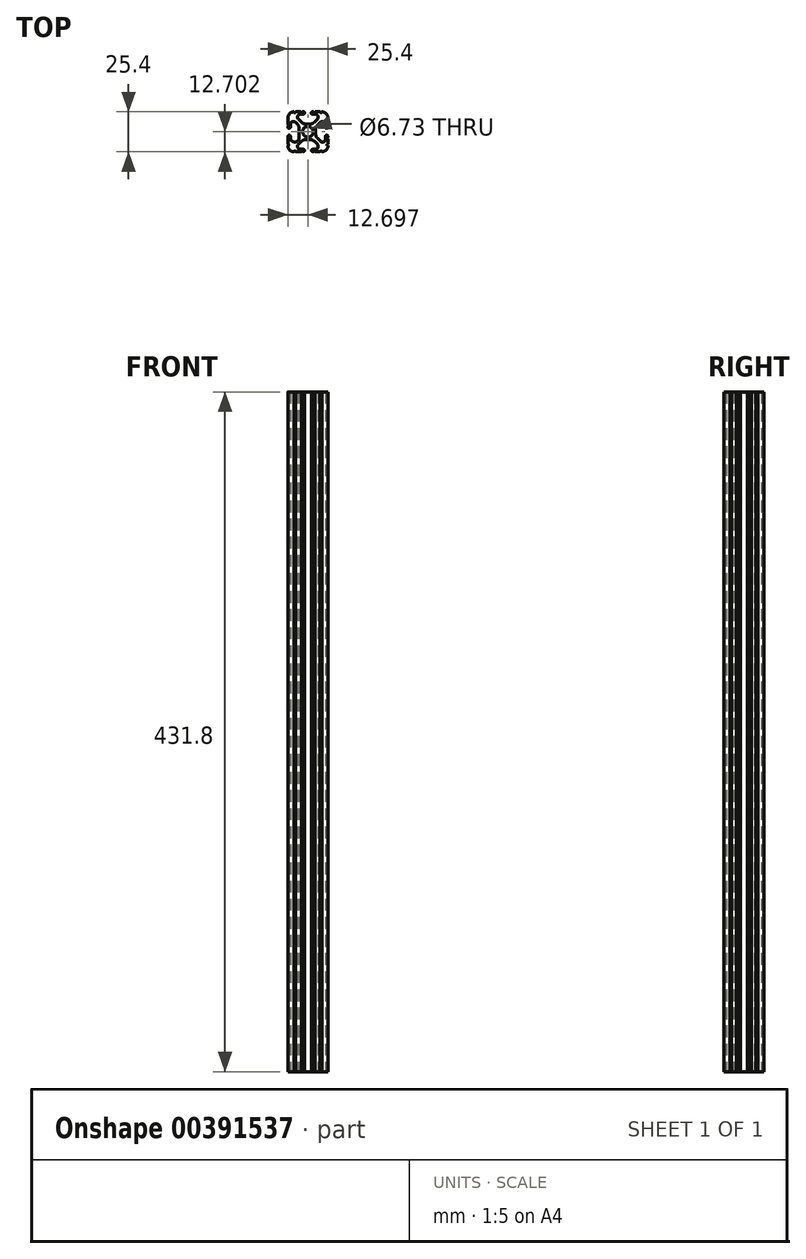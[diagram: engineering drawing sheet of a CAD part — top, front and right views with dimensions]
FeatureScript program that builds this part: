
annotation { "Feature Type Name" : "Feature", "Feature Type Description" : "" }
export const myFeature = defineFeature(function(context is Context, id is Id, definition is map)
    precondition{}
    {
        {
            var Q0;
            Q0=qCreatedBy(makeId("Top.planeOp"),FACE);
            var sketch = newSketch(context, id + "F0", { "sketchPlane" : qUnion([Q0])});
            skCircle(sketch, "E0", {"center": v(-11.44, 9.32) * mm, "radius": 3.36 * mm});
            skLineSegment(sketch, "E1.bottom", {"start": v(-9.99, 14.26) * mm, "end": v(-12.9, 14.26) * mm});
            skLineSegment(sketch, "E1.top", {"start": v(-9.99, 4.38) * mm, "end": v(-12.9, 4.38) * mm});
            skLineSegment(sketch, "E1.left", {"start": v(-6.5, 10.78) * mm, "end": v(-6.5, 7.86) * mm});
            skLineSegment(sketch, "E1.right", {"start": v(-16.98, 11.37) * mm, "end": v(-16.98, 5.6) * mm});
            skPoint(sketch, "E2.visualSharp", {"position": v(-24.14, 22.02) * mm});
            skPoint(sketch, "E3.visualSharp", {"position": v(1.26, 22.02) * mm});
            skPoint(sketch, "E4.visualSharp", {"position": v(1.26, -3.38) * mm});
            skPoint(sketch, "E5.visualSharp", {"position": v(-24.14, -3.38) * mm});
            skLineSegment(sketch, "E6.0", {"start": v(-17.44, 17.22) * mm, "end": v(-15.6, 15.38) * mm});
            skLineSegment(sketch, "E7.0", {"start": v(-19.34, 15.32) * mm, "end": v(-18.1, 14.07) * mm});
            skPoint(sketch, "E8.orphan", {"position": v(-22.6, -1.83) * mm});
            skPoint(sketch, "E9.orphan", {"position": v(-22.6, 20.47) * mm});
            skPoint(sketch, "E10.orphan", {"position": v(-0.3, 20.47) * mm});
            skPoint(sketch, "E11.orphan", {"position": v(-0.3, -1.83) * mm});
            skLineSegment(sketch, "E12", {"start": v(-7.3, 3.27) * mm, "end": v(-5.45, 1.42) * mm});
            skLineSegment(sketch, "E13.0", {"start": v(-17.44, 1.42) * mm, "end": v(-15.6, 3.27) * mm});
            skLineSegment(sketch, "E14.0", {"start": v(-7.3, 15.38) * mm, "end": v(-5.45, 17.22) * mm});
            skPoint(sketch, "E15.visualSharp", {"position": v(-22.6, 18.57) * mm});
            skArc(sketch, "E15.filletArc", {"start": v(-19.34, 15.32) * mm, "mid": v(-21.42, 15.73) * mm, "end": v(-22.6, 13.97) * mm});
            skPoint(sketch, "E16.visualSharp", {"position": v(-20.7, 20.47) * mm});
            skArc(sketch, "E16.filletArc", {"start": v(-16.1, 20.47) * mm, "mid": v(-17.85, 19.3) * mm, "end": v(-17.44, 17.22) * mm});
            skPoint(sketch, "E17.visualSharp", {"position": v(-4.09, 20.47) * mm});
            skLineSegment(sketch, "E18", {"start": v(-16.1, 20.47) * mm, "end": v(-14.33, 20.47) * mm});
            skLineSegment(sketch, "E19", {"start": v(-22.6, 13.97) * mm, "end": v(-22.6, 12.24) * mm});
            skLineSegment(sketch, "E20", {"start": v(-6.8, -1.83) * mm, "end": v(-8.53, -1.83) * mm});
            skArc(sketch, "E21.filletArc", {"start": v(-5.45, 17.22) * mm, "mid": v(-5.03, 19.3) * mm, "end": v(-6.8, 20.47) * mm});
            skPoint(sketch, "E22.visualSharp", {"position": v(-0.3, 0.08) * mm});
            skPoint(sketch, "E23.visualSharp", {"position": v(-2.2, -1.83) * mm});
            skArc(sketch, "E23.filletArc", {"start": v(-6.8, -1.83) * mm, "mid": v(-5.04, -0.65) * mm, "end": v(-5.45, 1.42) * mm});
            skArc(sketch, "E24.filletArc", {"start": v(-17.44, 1.42) * mm, "mid": v(-17.85, -0.65) * mm, "end": v(-16.1, -1.83) * mm});
            skArc(sketch, "E25.filletArc", {"start": v(-22.6, 5.6) * mm, "mid": v(-19.79, 2.8) * mm, "end": v(-16.98, 5.6) * mm});
            skLineSegment(sketch, "E26.bottom", {"start": v(-3.64, -3.38) * mm, "end": v(-6.8, -3.38) * mm});
            skLineSegment(sketch, "E26.top", {"start": v(-3.66, 22.02) * mm, "end": v(-6.8, 22.02) * mm});
            skLineSegment(sketch, "E26.left", {"start": v(1.26, 1.52) * mm, "end": v(1.26, 4.67) * mm});
            skArc(sketch, "E27.filletArc", {"start": v(-24.14, 0.43) * mm, "mid": v(-23.03, -2.26) * mm, "end": v(-20.33, -3.38) * mm});
            skArc(sketch, "E28.filletArc", {"start": v(-2.55, -3.38) * mm, "mid": v(0.14, -2.26) * mm, "end": v(1.26, 0.43) * mm});
            skArc(sketch, "E29.filletArc", {"start": v(1.26, 18.21) * mm, "mid": v(0.14, 20.9) * mm, "end": v(-2.55, 22.02) * mm});
            skArc(sketch, "E30.filletArc", {"start": v(-20.33, 22.02) * mm, "mid": v(-23.03, 20.9) * mm, "end": v(-24.14, 18.21) * mm});
            skPoint(sketch, "E31.newPointA", {"position": v(-16.38, 4.38) * mm});
            skArc(sketch, "E31.filletArc", {"start": v(-12.9, 4.38) * mm, "mid": v(-14.36, 4.1) * mm, "end": v(-15.6, 3.27) * mm});
            skPoint(sketch, "E32.newPointA", {"position": v(-6.5, 4.38) * mm});
            skArc(sketch, "E32.filletArc", {"start": v(-7.3, 3.27) * mm, "mid": v(-8.53, 4.1) * mm, "end": v(-9.99, 4.38) * mm});
            skArc(sketch, "E33.filletArc", {"start": v(-6.5, 7.86) * mm, "mid": v(-6.21, 6.4) * mm, "end": v(-5.39, 5.17) * mm});
            skArc(sketch, "E34.filletArc", {"start": v(-5.39, 13.47) * mm, "mid": v(-6.21, 12.24) * mm, "end": v(-6.5, 10.78) * mm});
            skPoint(sketch, "E35.newPointB", {"position": v(-6.5, 14.26) * mm});
            skArc(sketch, "E35.filletArc", {"start": v(-9.99, 14.26) * mm, "mid": v(-8.53, 14.55) * mm, "end": v(-7.3, 15.38) * mm});
            skPoint(sketch, "E36.newPointB", {"position": v(-16.38, 14.26) * mm});
            skArc(sketch, "E36.filletArc", {"start": v(-15.6, 15.38) * mm, "mid": v(-14.36, 14.55) * mm, "end": v(-12.9, 14.26) * mm});
            skArc(sketch, "E37.filletArc", {"start": v(-16.98, 11.37) * mm, "mid": v(-17.27, 12.83) * mm, "end": v(-18.1, 14.07) * mm});
            skLineSegment(sketch, "E38.filletArc", {"start": v(-16.98, 3.06) * mm, "end": v(-16.98, 3.06) * mm});
            skLineSegment(sketch, "E39", {"start": v(-5.39, 5.17) * mm, "end": v(-3.54, 3.33) * mm});
            skPoint(sketch, "E40.visualSharp", {"position": v(-0.3, 18.57) * mm});
            skArc(sketch, "E41.filletArc", {"start": v(-3.54, 3.33) * mm, "mid": v(-1.47, 2.91) * mm, "end": v(-0.3, 4.67) * mm});
            skLineSegment(sketch, "E42", {"start": v(-0.3, 4.67) * mm, "end": v(-0.3, 6.4) * mm});
            skLineSegment(sketch, "E43", {"start": v(-5.39, 13.47) * mm, "end": v(-3.54, 15.32) * mm});
            skArc(sketch, "E44.filletArc", {"start": v(-0.3, 13.97) * mm, "mid": v(-1.47, 15.73) * mm, "end": v(-3.54, 15.32) * mm});
            skArc(sketch, "E45", {"start": v(-22.6, 6.4) * mm, "mid": v(-23.37, 7.18) * mm, "end": v(-24.14, 6.4) * mm});
            skArc(sketch, "E46", {"start": v(-24.14, 12.24) * mm, "mid": v(-23.37, 11.48) * mm, "end": v(-22.6, 12.24) * mm});
            skArc(sketch, "E47", {"start": v(-14.36, 20.47) * mm, "mid": v(-13.57, 21.25) * mm, "end": v(-14.36, 22.02) * mm});
            skArc(sketch, "E48", {"start": v(-8.53, 22.02) * mm, "mid": v(-9.34, 21.25) * mm, "end": v(-8.53, 20.47) * mm});
            skArc(sketch, "E49", {"start": v(-0.3, 12.24) * mm, "mid": v(0.48, 11.5) * mm, "end": v(1.26, 12.24) * mm});
            skArc(sketch, "E50", {"start": v(1.26, 6.4) * mm, "mid": v(0.48, 7.13) * mm, "end": v(-0.3, 6.4) * mm});
            skArc(sketch, "E51", {"start": v(-8.53, -1.83) * mm, "mid": v(-9.14, -2.6) * mm, "end": v(-8.53, -3.38) * mm});
            skArc(sketch, "E52", {"start": v(-14.36, -3.38) * mm, "mid": v(-13.6, -2.6) * mm, "end": v(-14.36, -1.83) * mm});
            skLineSegment(sketch, "E53.trimOffspring", {"start": v(-14.36, -1.83) * mm, "end": v(-16.1, -1.83) * mm});
            skLineSegment(sketch, "E54.trimOffspring", {"start": v(-15.45, -3.38) * mm, "end": v(-19.23, -3.38) * mm});
            skLineSegment(sketch, "E55.trimOffspring", {"start": v(-0.3, 12.24) * mm, "end": v(-0.3, 13.97) * mm});
            skLineSegment(sketch, "E56.trimOffspring", {"start": v(1.26, 12.24) * mm, "end": v(1.26, 12.88) * mm});
            skLineSegment(sketch, "E57.trimOffspring", {"start": v(-22.6, 6.4) * mm, "end": v(-22.6, 5.6) * mm});
            skLineSegment(sketch, "E58.trimOffspring", {"start": v(-24.14, 12.24) * mm, "end": v(-24.14, 12.88) * mm});
            skLineSegment(sketch, "E59.trimOffspring", {"start": v(-8.6, 20.47) * mm, "end": v(-6.8, 20.47) * mm});
            skLineSegment(sketch, "E60.trimOffspring", {"start": v(-14.33, 22.02) * mm, "end": v(-15, 22.02) * mm});
            skPoint(sketch, "E61.start.orphan", {"position": v(-14.36, 14.55) * mm});
            skPoint(sketch, "E62.start.orphan", {"position": v(-8.53, 14.55) * mm});
            skPoint(sketch, "E63.start.orphan", {"position": v(-6.21, 12.24) * mm});
            skPoint(sketch, "E64.start.orphan", {"position": v(-6.21, 6.4) * mm});
            skPoint(sketch, "E65.start.orphan", {"position": v(-17.27, 12.83) * mm});
            skPoint(sketch, "E66.start.orphan", {"position": v(-16.98, 3.06) * mm});
            skPoint(sketch, "E67.start.orphan", {"position": v(-8.53, 4.1) * mm});
            skPoint(sketch, "E68.start.orphan", {"position": v(-14.36, 4.1) * mm});
            skPoint(sketch, "E69.endSnap0", {"position": v(1.26, 15.22) * mm});
            skPoint(sketch, "E70.startSnap0", {"position": v(-0.3, 5.54) * mm});
            skArc(sketch, "E71", {"start": v(-3.66, 22.02) * mm, "mid": v(-3.1, 21.53) * mm, "end": v(-2.55, 22.02) * mm});
            skArc(sketch, "E72", {"start": v(-7.89, 22.02) * mm, "mid": v(-7.34, 21.48) * mm, "end": v(-6.8, 22.02) * mm});
            skArc(sketch, "E73", {"start": v(-16.1, 22.02) * mm, "mid": v(-15.54, 21.48) * mm, "end": v(-15, 22.02) * mm});
            skArc(sketch, "E74", {"start": v(-20.33, 22.02) * mm, "mid": v(-19.78, 21.47) * mm, "end": v(-19.23, 22.02) * mm});
            skLineSegment(sketch, "E75", {"start": v(-24.14, 18.21) * mm, "end": v(-24.14, 17.13) * mm});
            skArc(sketch, "E76", {"start": v(-24.14, 12.88) * mm, "mid": v(-23.59, 13.42) * mm, "end": v(-24.14, 13.97) * mm});
            skArc(sketch, "E77", {"start": v(-24.14, 0.43) * mm, "mid": v(-23.59, 0.98) * mm, "end": v(-24.14, 1.53) * mm});
            skArc(sketch, "E78", {"start": v(-19.23, -3.38) * mm, "mid": v(-19.78, -2.82) * mm, "end": v(-20.33, -3.38) * mm});
            skArc(sketch, "E79", {"start": v(-14.36, -3.38) * mm, "mid": v(-14.9, -2.84) * mm, "end": v(-15.45, -3.38) * mm});
            skArc(sketch, "E80", {"start": v(-6.8, -3.38) * mm, "mid": v(-7.35, -2.83) * mm, "end": v(-7.9, -3.38) * mm});
            skArc(sketch, "E81", {"start": v(-2.55, -3.38) * mm, "mid": v(-3.1, -2.83) * mm, "end": v(-3.64, -3.38) * mm});
            skLineSegment(sketch, "E82.trimOffspring", {"start": v(-16.1, 22.02) * mm, "end": v(-19.23, 22.02) * mm});
            skLineSegment(sketch, "E83.trimOffspring", {"start": v(-24.14, 13.97) * mm, "end": v(-24.14, 18.21) * mm});
            skLineSegment(sketch, "E84.trimOffspring", {"start": v(-24.14, 5.77) * mm, "end": v(-24.14, 6.4) * mm});
            skLineSegment(sketch, "E85.trimOffspring", {"start": v(-7.9, -3.38) * mm, "end": v(-8.53, -3.38) * mm});
            skArc(sketch, "E86", {"start": v(1.26, 1.52) * mm, "mid": v(0.72, 0.98) * mm, "end": v(1.26, 0.43) * mm});
            skArc(sketch, "E87", {"start": v(1.26, 5.77) * mm, "mid": v(0.71, 5.22) * mm, "end": v(1.26, 4.67) * mm});
            skLineSegment(sketch, "E88.trimOffspring", {"start": v(1.26, 5.77) * mm, "end": v(1.26, 6.4) * mm});
            skArc(sketch, "E89", {"start": v(1.26, 18.21) * mm, "mid": v(0.7, 17.66) * mm, "end": v(1.26, 17.12) * mm});
            skArc(sketch, "E90", {"start": v(1.26, 13.97) * mm, "mid": v(0.71, 13.42) * mm, "end": v(1.26, 12.88) * mm});
            skLineSegment(sketch, "E91.trimOffspring", {"start": v(1.26, 13.97) * mm, "end": v(1.26, 17.12) * mm});
            skLineSegment(sketch, "E92.trimOffspring", {"start": v(-7.89, 22.02) * mm, "end": v(-8.6, 22.02) * mm});
            skLineSegment(sketch, "E93", {"start": v(-24.14, 5.77) * mm, "end": v(-24.14, 1.53) * mm});
            skPoint(sketch, "E94.orphan", {"position": v(-23.2, 5.6) * mm});
            skSolve(sketch);
        }
        {
            var Q0;
            Q0=qSketchRegion(id+"F0",true);
            extrude(context, id + "F1", {"entities" : qUnion([Q0]), "endBound" : BoundingType.SYMMETRIC, "depth" : 431.8 * mm});
        }
    });
